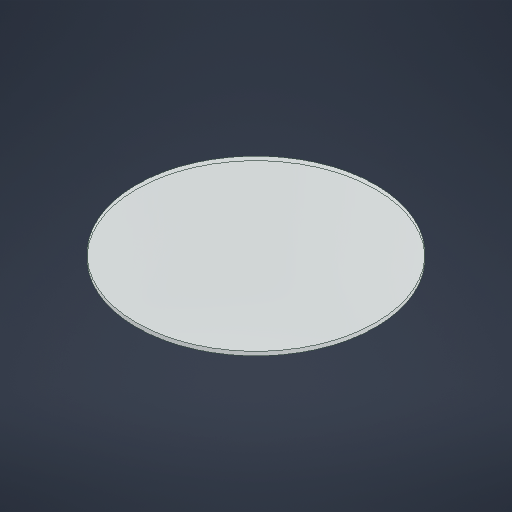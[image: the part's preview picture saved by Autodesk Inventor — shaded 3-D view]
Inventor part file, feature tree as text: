
AUTODESK INVENTOR PART (.ipt)
format: ipt  version: 2025 (Build 290162000, 162)  size: 187,392 bytes
history: native  units: in
note: dims shown in document units (in); Inventor stores cm internally (conversion verified against a paired STEP export)
features: extrude x1, sketch x1
ambient origin geometry x8: Origin, YZ Plane, XZ Plane, XY Plane, X Axis, Y Axis, Z Axis, Center Point
bodies: Solid1 (feature_tree)
feature tree (2):
  extrude  "Extrusion1"  Depth=0.1575in TaperAngle=0.0deg
  sketch  "Sketch1"  dims[d0=9.4488in d1=0.1575in d2=0.0in]
